# Revit family: lf-300_500x2-(f)60_60Hz
name_source: partatom
category: 機械設備
units: mm (PartAtom-declared; Revit-internal decimal feet)

## family parameters
OmniClass タイトル = Heat Exchangers for Ventilation Air
OmniClass 番号 = 23.75.10.34.21
パーツ タイプ = 標準
ロード時にボイドで切り取り = いいえ
丸型コネクタ寸法 = 直径を使用
作業面ベース = いいえ
共有 = いいえ
常に垂直 = はい
部屋計算ポイント = はい

## types (6) — shared parameters
Clearance Right = 600
D1 = 1840  [stored 6.03675 ft]
Depth = 1750  [stored 5.74147 ft]
Duct_Height = 80  [stored 0.262467 ft]
Duct_Pitch1 = 479  [stored 1.57152 ft]
Duct_Pitch2 = 458
EAサイズ_D = 298  [stored 0.97769 ft]
EAサイズ_W = 748  [stored 2.45407 ft]
H1 = 90  [stored 0.295276 ft]
IfcExportAs = IfcAirToAirHeatRecoveryType
IfcExportType = ROTARYWHEEL
MID静圧 = 0.0 Pa
MID風量 = 0.0 m³/h
MIN静圧 = 0.0 Pa
MIN風量 = 0.0 m³/h
OAサイズ_D = 298  [stored 0.97769 ft]
OAサイズ_W = 748  [stored 2.45407 ft]
OmniClassCode = 23-27 23 19 11
RAサイズ_D = 298  [stored 0.97769 ft]
RAサイズ_W = 748  [stored 2.45407 ft]
SAサイズ_D = 298  [stored 0.97769 ft]
SAサイズ_W = 748  [stored 2.45407 ft]
URL = https://www.mitsubishielectric.co.jp
Uniclass2015Code = Pr_60_60_36_88
Uniclass2015Title = Thermal wheels
Uniclass2015Version = Systems v1.9
W1 = 1170  [stored 3.83858 ft]
Width = 1220  [stored 4.00262 ft]
エンタルピ交換効率_冷房 = 65.00%
エンタルピ交換効率_暖房 = 68.00%
メンテナンススペース = はい
仕様書バージョン = Version1.0
企業コード = 108420
分類コード = 50052504100050
初期抵抗 = 0.0 Pa
参照している仕様書等のバージョン = 公共建築工事標準仕様書（機械設備工事編）平成31年度版
周波数 = 60 Hz
呼称 = 全熱交換ユニット
外気量 = 0.0 m³/h
実風量 = 0.0 m³/h
形式 = 床置形
排気量 = 0.0 m³/h
本体マテリアル = 溶融亜鉛めっき鋼板
本体固定用穴_径 = 20  [stored 0.0656168 ft]
本体固定用穴ピッチ1 = 568  [stored 1.86352 ft]
本体固定用穴ピッチ2 = 850  [stored 2.78871 ft]
極数 = 3
法定耐用年数 = 15
温度交換効率 = 75.00%
相 = 3
積算_科目 = 1 空気調和設備
符号 = HEU
製品リリース年月 = 2018/7/25
製品出荷対象 = 国内
製造元 = 三菱電機株式会社
設置方法 = 床置形
設計風量 = 0.0 m³/h
負荷分類 = 3_ファン類
運転質量 = 0.00 kg
電動機出力 = 0 W
電圧 = 200 V
zero-valued in all types: Clearance Back, Clearance Bottom, Clearance Front, Clearance Left, Clearance Top

## per-type parameters (varying)
| type | Height | MAX静圧 | MAX風量 | 価格 | 機外静圧 | 機外静圧_排気 | 消費電力 | 製品質量 | 説明 | 質量 | 面風速 | 風量 | 騒音レベル(dB(A)) |
| LF-300X2-60 | 1800  [stored 5.90551 ft] | 320.0 Pa | 3000.0 m³/h | 3813000 $ | 320.0 Pa | 320.0 Pa | 2500 W | 540.00 kg | 設備用ロスナイ 床置形 | 648.00 kg | 3.7 m/s | 3000.0 m³/h | 52 |
| LF-400X2-60 | 1800  [stored 5.90551 ft] | 300.0 Pa | 4000.0 m³/h | 4538000 $ | 300.0 Pa | 300.0 Pa | 3000 W | 550.00 kg | 設備用ロスナイ 床置形 | 660.00 kg | 4.9 m/s | 4000.0 m³/h | 53.5 |
| LF-500X2-60 | 2187  [stored 7.1752 ft] | 215.0 Pa | 5000.0 m³/h | 5325000 $ | 215.0 Pa | 215.0 Pa | 3560 W | 620.00 kg | 設備用ロスナイ 床置形 | 744.00 kg | 6.2 m/s | 5000.0 m³/h | 54.5 |
| LF-300X2-F60 | 1800  [stored 5.90551 ft] | 320.0 Pa | 3000.0 m³/h | 4194000 $ | 320.0 Pa | 320.0 Pa | 2500 W | 540.00 kg | 設備用ロスナイ 床置形 インバータ端子付 | 648.00 kg | 3.7 m/s | 3000.0 m³/h | 52 |
| LF-400X2-F60 | 1800  [stored 5.90551 ft] | 330.0 Pa | 4000.0 m³/h | 4993000 $ | 330.0 Pa | 330.0 Pa | 3000 W | 550.00 kg | 設備用ロスナイ 床置形 インバータ端子付 | 660.00 kg | 4.9 m/s | 4000.0 m³/h | 53.5 |
| LF-500X2-F60 | 2187  [stored 7.1752 ft] | 215.0 Pa | 5000.0 m³/h | 5858000 $ | 215.0 Pa | 215.0 Pa | 3560 W | 620.00 kg | 設備用ロスナイ 床置形 インバータ端子付 | 744.00 kg | 6.2 m/s | 5000.0 m³/h | 54.5 |

note: column(s) folded — value = type name in every type: モデル

note: [stored X ft] marks values corroborated as IEEE doubles in the binary element streams (Revit-internal decimal feet)
